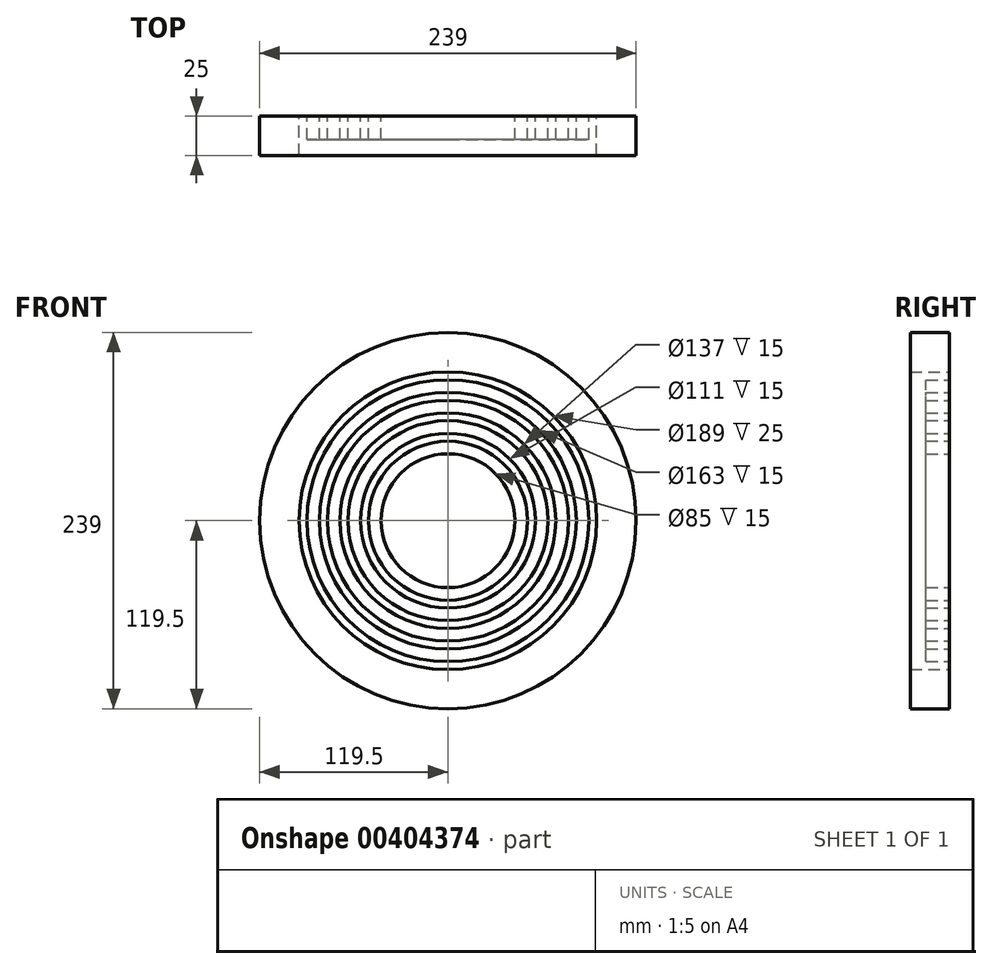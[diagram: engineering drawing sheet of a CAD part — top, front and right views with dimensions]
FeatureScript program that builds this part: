
annotation { "Feature Type Name" : "Feature", "Feature Type Description" : "" }
export const myFeature = defineFeature(function(context is Context, id is Id, definition is map)
    precondition{}
    {
        {
            var Q0;
            Q0=qCreatedBy(makeId("Front.planeOp"),FACE);
            var sketch = newSketch(context, id + "F0", { "sketchPlane" : qUnion([Q0])});
            skCircle(sketch, "E0", {"center": v(0, 0) * mm, "radius": 42.5 * mm});
            skCircle(sketch, "E1", {"center": v(0, 0) * mm, "radius": 50.5 * mm});
            skSolve(sketch);
        }
        {
            var Q0;
            Q0 = qSketchRegion(id + "F0", true);
            extrude(context, id + "F1", {"entities" : qUnion([Q0]), "depth" : 15 * mm});
        }
        {
            var Q0;
            Q0=qCreatedBy(makeId("Front.planeOp"),FACE);
            var sketch = newSketch(context, id + "F2", { "sketchPlane" : qUnion([Q0])});
            skCircle(sketch, "E2", {"center": v(0, 0) * mm, "radius": 55.5 * mm});
            skCircle(sketch, "E3", {"center": v(0, 0) * mm, "radius": 63.5 * mm});
            skCircle(sketch, "E4.0", {"center": v(0, 0) * mm, "radius": 50.5 * mm});
            skSolve(sketch);
        }
        {
            var Q0;
            Q0=makeQuery(id+"F2.imprint","IMPRINT",FACE,{"disambiguationData":[TD([[makeQuery(id+"F2.imprint","IMPRINT",EDGE,{"derivedFrom":sQuery(id+"F2.wireOp",EDGE,"E2")}),-1.0]])]});
            extrude(context, id + "F3", {"entities" : qUnion([Q0]), "depth" : 15 * mm});
        }
        {
            var Q0;
            Q0=qCreatedBy(makeId("Front.planeOp"),FACE);
            var sketch = newSketch(context, id + "F4", { "sketchPlane" : qUnion([Q0])});
            skCircle(sketch, "E5", {"center": v(0, 0) * mm, "radius": 68.5 * mm});
            skCircle(sketch, "E6", {"center": v(0, 0) * mm, "radius": 76.5 * mm});
            skSolve(sketch);
        }
        {
            var Q0;
            Q0 = qSketchRegion(id + "F4", true);
            extrude(context, id + "F5", {"entities" : qUnion([Q0]), "depth" : 15 * mm});
        }
        {
            var Q0;
            Q0=qCreatedBy(makeId("Front.planeOp"),FACE);
            var sketch = newSketch(context, id + "F6", { "sketchPlane" : qUnion([Q0])});
            skCircle(sketch, "E7", {"center": v(0, 0) * mm, "radius": 81.5 * mm});
            skCircle(sketch, "E8", {"center": v(0, 0) * mm, "radius": 89.5 * mm});
            skSolve(sketch);
        }
        {
            var Q0;
            Q0 = qSketchRegion(id + "F6", true);
            extrude(context, id + "F7", {"entities" : qUnion([Q0]), "depth" : 15 * mm});
        }
        {
            var Q0;
            Q0=qCreatedBy(makeId("Front.planeOp"),FACE);
            var sketch = newSketch(context, id + "F8", { "sketchPlane" : qUnion([Q0])});
            skCircle(sketch, "E9", {"center": v(0, 0) * mm, "radius": 94.5 * mm});
            skCircle(sketch, "E10", {"center": v(0, 0) * mm, "radius": 119.5 * mm});
            skSolve(sketch);
        }
        {
            var Q0;
            Q0=makeQuery(id+"F8.imprint","IMPRINT",FACE,{"disambiguationData":[TD([[makeQuery(id+"F8.imprint","IMPRINT",EDGE,{"derivedFrom":sQuery(id+"F8.wireOp",EDGE,"E9")}),-1.0]])]});
            extrude(context, id + "F9", {"entities" : qUnion([Q0]), "depth" : 25 * mm});
        }
    });
